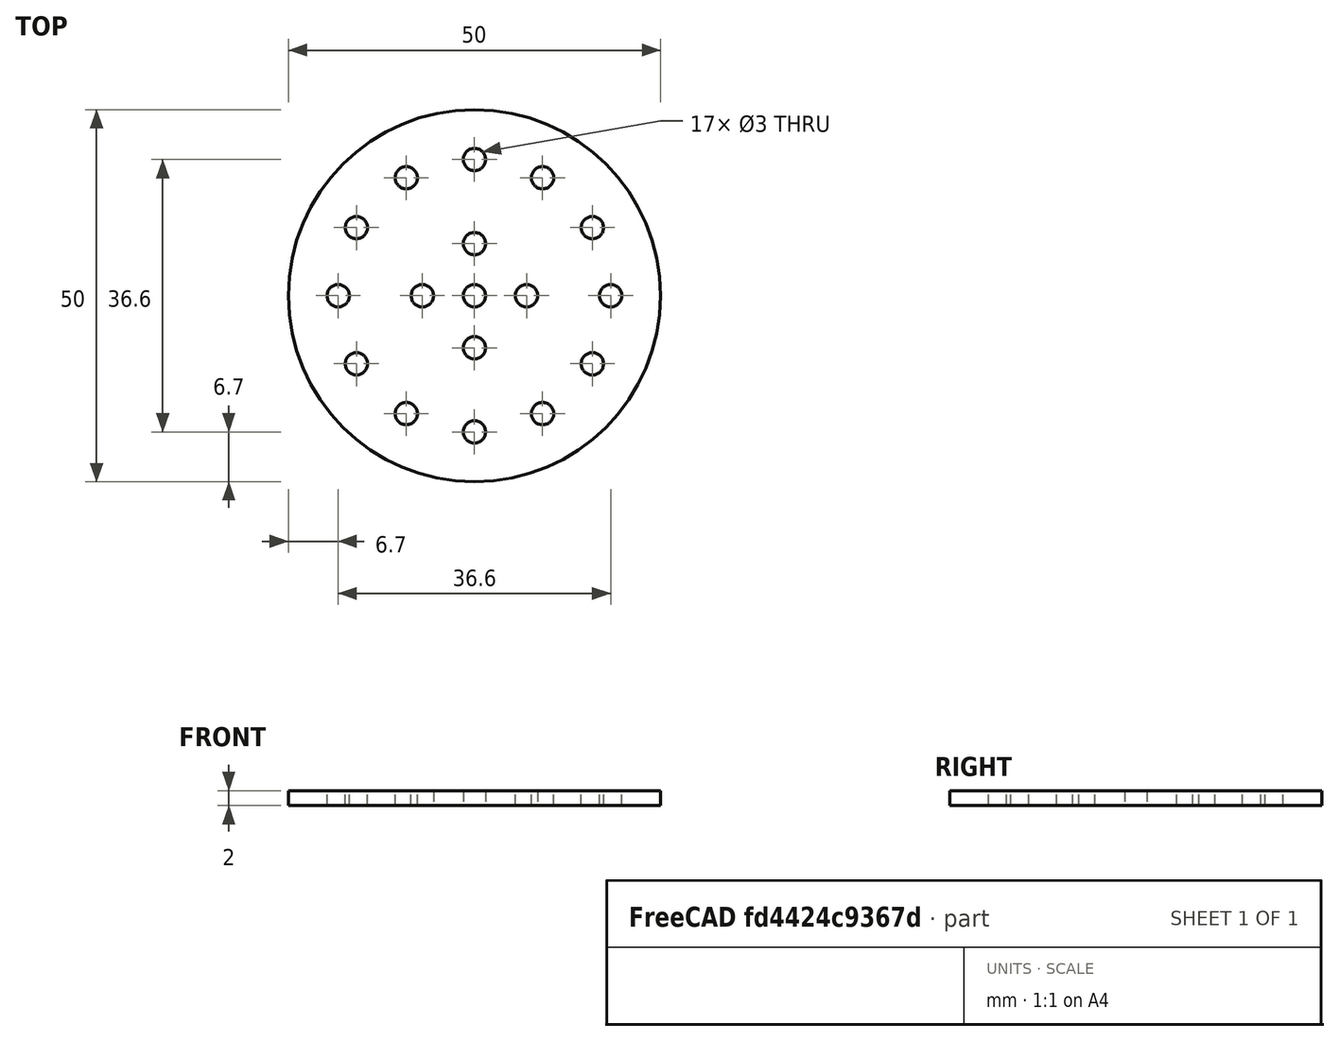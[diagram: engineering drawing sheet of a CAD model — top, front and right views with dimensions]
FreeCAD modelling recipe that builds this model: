
FCSTD DOCUMENT  (FreeCAD 0.20R29177 +426 (Git))
Label: servo_spinner
License: All rights reserved
LicenseURL: http://en.wikipedia.org/wiki/All_rights_reserved
objects: Sketcher::SketchObject×3, PartDesign::Pocket×2, PartDesign::Pad×1, Mesh::Feature×1, PartDesign::PolarPattern×1, PartDesign::Body×1
note: 11 computed .brp shape members not serialized (recipe doc carries the construction recipe); baked Part::Feature solids carry a one-line shape summary decoded from their .brp

FEATURE [Sketcher::SketchObject] Sketch
  FullyConstrained = true
  MapMode = 5
  Support = -> [XY_Plane]
  sketch-geometry (1):
    g0: Circle CenterX=0 CenterY=0 CenterZ=0 NormalX=0 NormalY=0 NormalZ=1 AngleXU=0 Radius=25
  constraints (2):
    c: Coincident(g0,g-1)
    c: Radius(g0) = 25
FEATURE [PartDesign::Pad] Pad
  Direction = (0,0,1)
  Length = 2
  Length2 = 10
  Profile = -> Sketch
  ReferenceAxis = -> Sketch [N_Axis]
  Type = 0
FEATURE [Sketcher::SketchObject] Sketch001
  FullyConstrained = true
  MapMode = 5
  Support = -> [XY_Plane]
  sketch-geometry (5):
    g0: Circle CenterX=0 CenterY=-4e-16 CenterZ=0 NormalX=0 NormalY=0 NormalZ=1 AngleXU=0 Radius=1.5
    g1: Circle CenterX=0 CenterY=7 CenterZ=0 NormalX=0 NormalY=0 NormalZ=1 AngleXU=0 Radius=1.5
    g2: Circle CenterX=-7 CenterY=0 CenterZ=0 NormalX=0 NormalY=0 NormalZ=1 AngleXU=0 Radius=1.5
    g3: Circle CenterX=7 CenterY=0 CenterZ=0 NormalX=0 NormalY=0 NormalZ=1 AngleXU=0 Radius=1.5
    g4: Circle CenterX=0 CenterY=-7 CenterZ=0 NormalX=0 NormalY=0 NormalZ=1 AngleXU=0 Radius=1.5
  constraints (12):
    c: Coincident(g0,g-1)
    c: Radius(g0) = 1.5
    c: PointOnObject(g1,g-2)
    c: Radius(g1) = 1.5
    c: PointOnObject(g2,g-1)
    c: Radius(g2) = 1.5
    c: Radius(g3) = 1.5
    c: Radius(g4) = 1.5
    c: DistanceY(g4,g1) = 14
    c: DistanceX(g2,g3) = 14
    c: Symmetric(g2,g3,g0)
    c: Symmetric(g1,g4,g0)
FEATURE [Mesh::Feature] BottomRace
FEATURE [PartDesign::Pocket] Pocket
  BaseFeature = -> Pad
  Direction = (0,0,-1)
  Length = 5
  Length2 = 5
  Midplane = true
  Profile = -> Sketch001
  ReferenceAxis = -> Sketch001 [N_Axis]
  Type = 1
FEATURE [Sketcher::SketchObject] Sketch002
  FullyConstrained = true
  MapMode = 5
  Support = -> [XY_Plane]
  sketch-geometry (1):
    g0: Circle CenterX=0 CenterY=18.3 CenterZ=0 NormalX=0 NormalY=0 NormalZ=1 AngleXU=0 Radius=1.5
  constraints (3):
    c: PointOnObject(g0,g-2)
    c: DistanceY(g-1,g0) = 18.3
    c: Radius(g0) = 1.5
FEATURE [PartDesign::Pocket] Pocket001
  BaseFeature = -> Pocket
  Direction = (0,0,-1)
  Length = 5
  Length2 = 5
  Midplane = true
  Profile = -> Sketch002
  ReferenceAxis = -> Sketch002 [N_Axis]
  Type = 1
FEATURE [PartDesign::PolarPattern] PolarPattern
  Angle = 360
  Axis = -> Sketch002 [N_Axis]
  BaseFeature = -> Pocket001
  Occurrences = 12
  Originals = -> [Pocket001]
FEATURE [PartDesign::Body] Body
  Group = -> [Sketch,Pad,Sketch001,Pocket,Sketch002,Pocket001,PolarPattern]
  Origin = -> Origin
  Tip = -> PolarPattern
